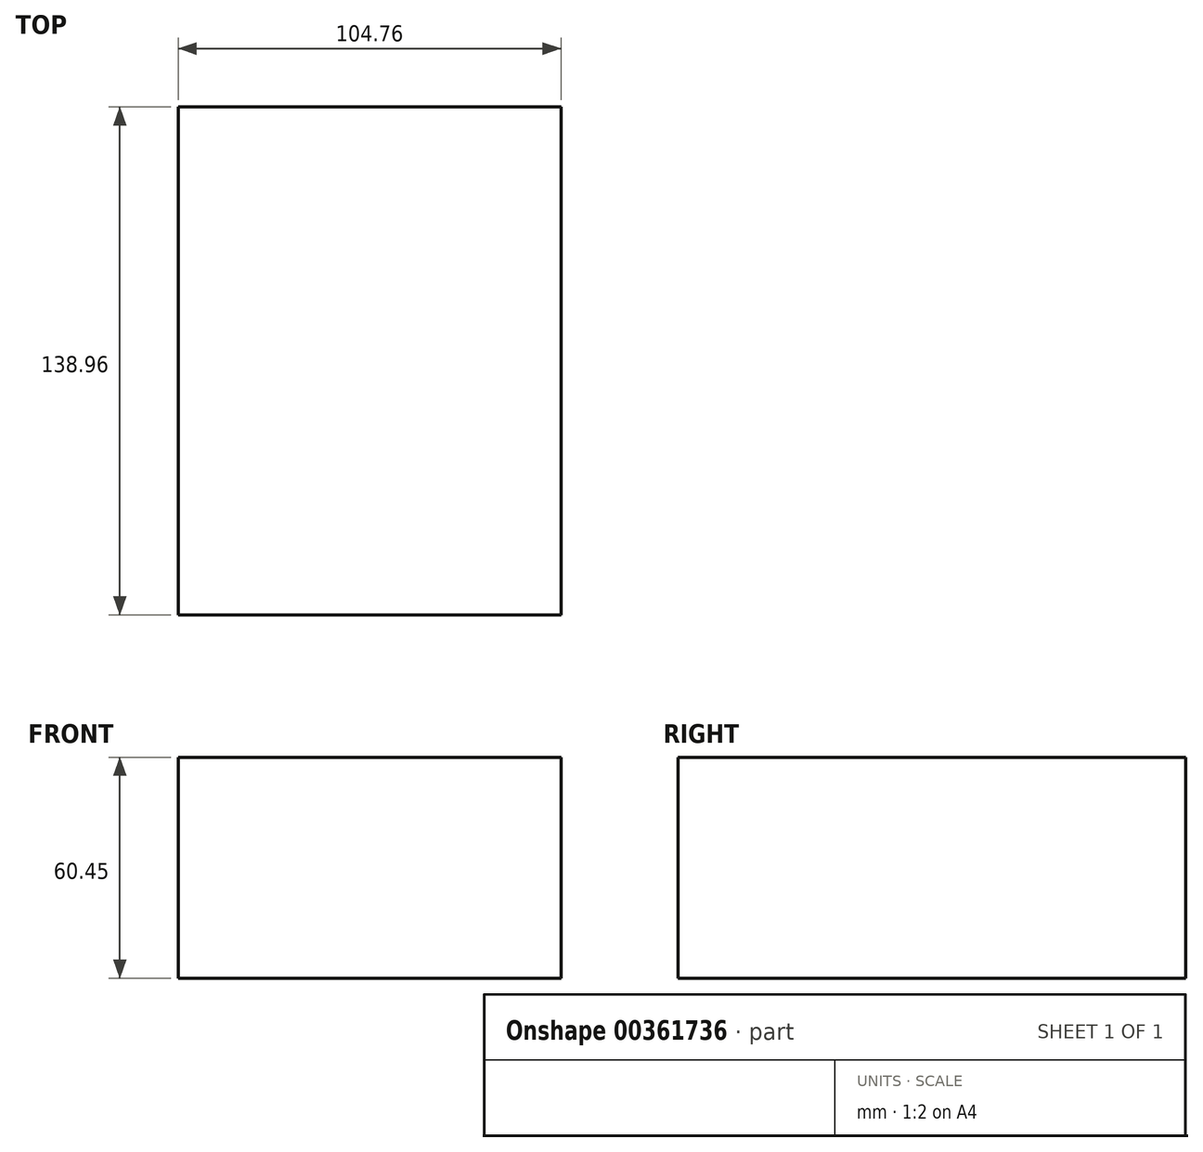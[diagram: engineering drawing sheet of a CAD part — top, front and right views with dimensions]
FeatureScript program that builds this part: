
annotation { "Feature Type Name" : "Feature", "Feature Type Description" : "" }
export const myFeature = defineFeature(function(context is Context, id is Id, definition is map)
    precondition{}
    {
        {
            var Q0;
            Q0=qCreatedBy(makeId("Top.planeOp"),FACE);
            var sketch = newSketch(context, id + "F0", { "sketchPlane" : qUnion([Q0])});
            skLineSegment(sketch, "E0.bottom", {"start": v(-42, -42.05) * mm, "end": v(62.76, -42.05) * mm});
            skLineSegment(sketch, "E0.top", {"start": v(-42, 96.9) * mm, "end": v(62.76, 96.9) * mm});
            skLineSegment(sketch, "E0.left", {"start": v(-42, -42.05) * mm, "end": v(-42, 96.9) * mm});
            skLineSegment(sketch, "E0.right", {"start": v(62.76, -42.05) * mm, "end": v(62.76, 96.9) * mm});
            skSolve(sketch);
        }
        {
            var Q0;
            Q0 = qSketchRegion(id + "F0", true);
            extrude(context, id + "F1", {"entities" : qUnion([Q0]), "depth" : 60.45 * mm});
        }
    });
